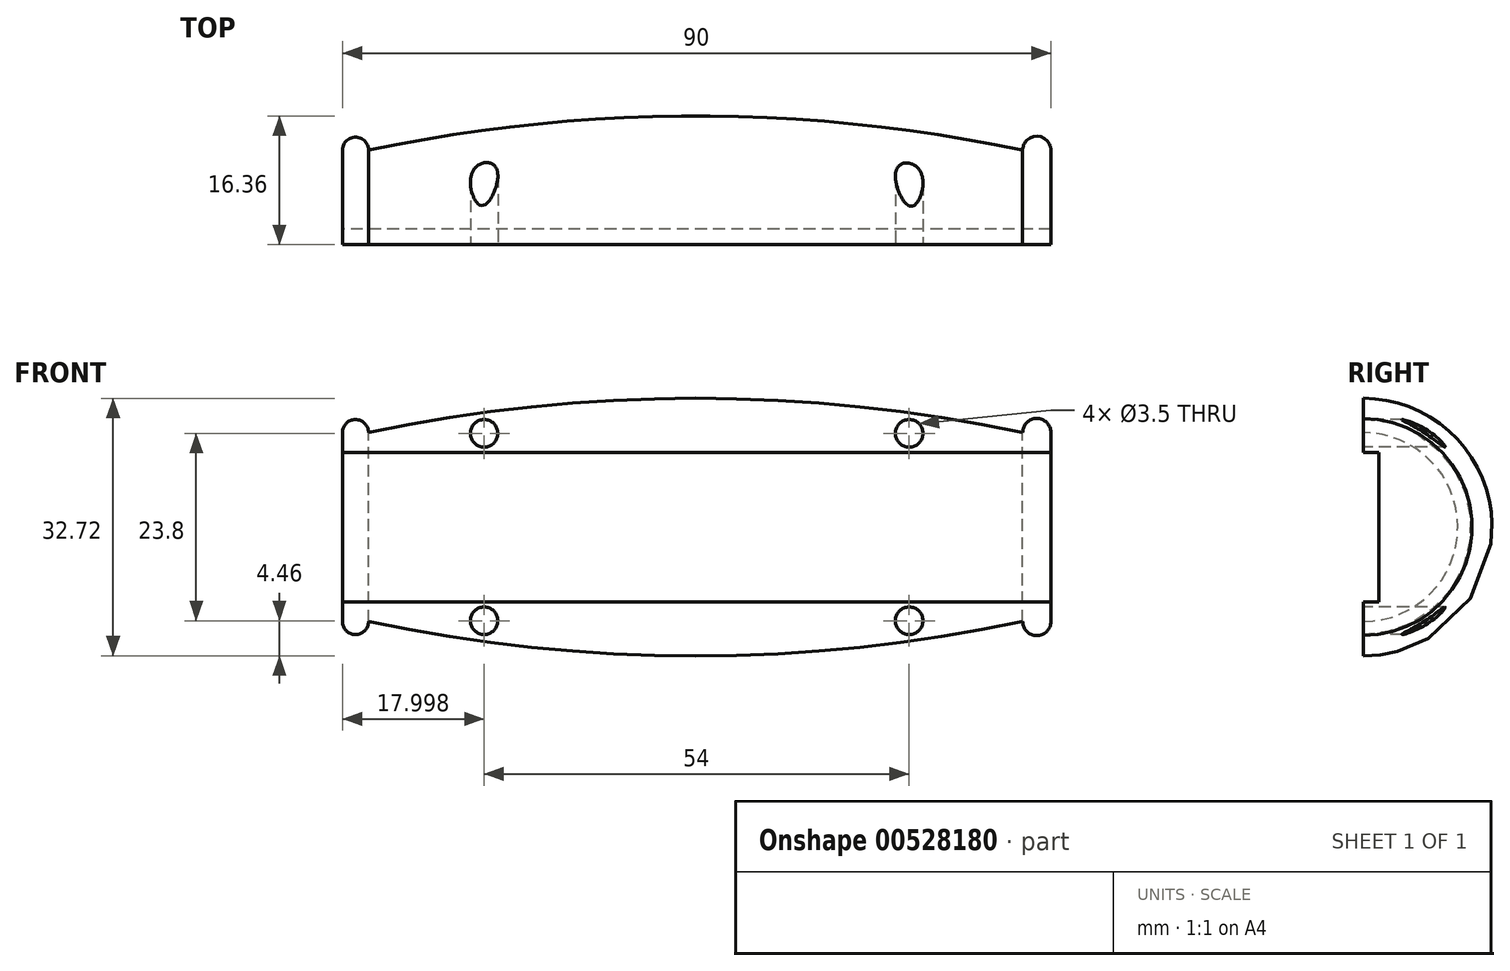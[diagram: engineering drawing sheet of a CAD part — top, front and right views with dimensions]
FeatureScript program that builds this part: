
annotation { "Feature Type Name" : "Feature", "Feature Type Description" : "" }
export const myFeature = defineFeature(function(context is Context, id is Id, definition is map)
    precondition{}
    {
        {
            var Q0;
            Q0=qCreatedBy(makeId("Front.planeOp"),FACE);
            var sketch = newSketch(context, id + "F0", { "sketchPlane" : qUnion([Q0])});
            skLineSegment(sketch, "E0", {"start": v(-128.4, 0) * mm, "end": v(-128.4, 12) * mm});
            skArc(sketch, "E1", {"start": v(-125.07, 12) * mm, "mid": v(-126.73, 13.66) * mm, "end": v(-128.4, 12) * mm});
            skLineSegment(sketch, "E2", {"start": v(-38.4, 12) * mm, "end": v(-38.4, 0) * mm});
            skLineSegment(sketch, "E3", {"start": v(-38.4, 0) * mm, "end": v(-128.4, 0) * mm});
            skArc(sketch, "E4", {"start": v(-38.4, 12) * mm, "mid": v(-40.19, 13.8) * mm, "end": v(-41.98, 12) * mm});
            skArc(sketch, "E5", {"start": v(-41.98, 12) * mm, "mid": v(-83.52, 16.36) * mm, "end": v(-125.07, 12) * mm});
            skSolve(sketch);
        }
        {
            var Q0;
            Q0=makeQuery(id+"F0.imprint","IMPRINT",FACE,{"disambiguationData":[TD([[makeQuery(id+"F0.imprint","IMPRINT",EDGE,{"derivedFrom":sQuery(id+"F0.wireOp",EDGE,"E0")}),-1.0]])]});
            var Q1;
            Q1=sQuery(id+"F0.wireOp",EDGE,"E3");
            revolve(context, id + "F1", {"entities" : qUnion([Q0]), "axis" : qUnion([Q1]), "revolveType" : RevolveType.ONE_DIRECTION, "angle" : 180 * degree});
        }
        {
            var Q0;
            Q0=makeQuery(id+"F1.opRevolve","SWEPT_FACE",FACE,{"disambiguationData":[OSD([sQuery(id+"F0.wireOp",EDGE,"E0")])]});
            var sketch = newSketch(context, id + "F2", { "sketchPlane" : qUnion([Q0])});
            skLineSegment(sketch, "E6", {"start": v(0, -9.5) * mm, "end": v(-2, -9.5) * mm});
            skLineSegment(sketch, "E7", {"start": v(-2, -9.5) * mm, "end": v(-2, 9.5) * mm});
            skLineSegment(sketch, "E8", {"start": v(-2, 9.5) * mm, "end": v(0, 9.5) * mm});
            skLineSegment(sketch, "E9", {"start": v(0, -9.5) * mm, "end": v(0, 9.5) * mm});
            skSolve(sketch);
        }
        {
            var Q0;
            Q0=makeQuery(id+"F2.imprint","IMPRINT",FACE,{"disambiguationData":[TD([[makeQuery(id+"F2.imprint","IMPRINT",EDGE,{"derivedFrom":sQuery(id+"F2.wireOp",EDGE,"E6")}),-1.0]])]});
            extrude(context, id + "F3", {"entities" : qUnion([Q0]), "operationType" : NewBodyOperationType.REMOVE, "oppositeDirection" : true, "depth" : 90 * mm, "offsetDistance" : 25 * mm});
        }
        {
            var Q0;
            {var subQ0=sQuery(id+"F0.wireOp",EDGE,"E4");var subQ1=sQuery(id+"F0.wireOp",EDGE,"E2");var subQ2=sQuery(id+"F0.wireOp",EDGE,"E1");var subQ3=sQuery(id+"F0.wireOp",EDGE,"E0");var subQ4=sQuery(id+"F0.wireOp",EDGE,"E5");Q0=makeQuery(id+"F3.boolean.opBoolean","SPLIT",FACE,{"disambiguationData":[TD([makeQuery(id+"F3.opExtrude","SWEPT_FACE",FACE,{"disambiguationData":[OSD([sQuery(id+"F2.wireOp",EDGE,"E8")])]})])],"derivedFrom":makeQuery(id+"F1.opRevolve","CAP_FACE",FACE,{"disambiguationData":[OSD([subQ3,subQ2,subQ1,sQuery(id+"F0.wireOp",EDGE,"E3"),subQ0,subQ4])],"isStart":true})});}
            var sketch = newSketch(context, id + "F4", { "sketchPlane" : qUnion([Q0])});
            skLineSegment(sketch, "E10", {"start": v(-128.4, 11.9) * mm, "end": v(-110.4, 11.9) * mm, "construction": true});
            skLineSegment(sketch, "E11", {"start": v(-128.4, 11.9) * mm, "end": v(-128.4, 9.5) * mm, "construction": true});
            skCircle(sketch, "E12", {"center": v(-110.4, 11.9) * mm, "radius": 1.75 * mm});
            skLineSegment(sketch, "E13", {"start": v(-38.4, 9.5) * mm, "end": v(-38.4, 11.9) * mm, "construction": true});
            skLineSegment(sketch, "E14", {"start": v(-38.4, 11.9) * mm, "end": v(-56.4, 11.9) * mm, "construction": true});
            skCircle(sketch, "E15", {"center": v(-56.4, 11.9) * mm, "radius": 1.75 * mm});
            skSolve(sketch);
        }
        {
            var Q0;
            {var subQ0=sQuery(id+"F0.wireOp",EDGE,"E4");var subQ1=sQuery(id+"F0.wireOp",EDGE,"E2");var subQ2=sQuery(id+"F0.wireOp",EDGE,"E1");var subQ3=sQuery(id+"F0.wireOp",EDGE,"E0");var subQ4=sQuery(id+"F0.wireOp",EDGE,"E5");Q0=makeQuery(id+"F3.boolean.opBoolean","SPLIT",FACE,{"disambiguationData":[TD([makeQuery(id+"F3.opExtrude","SWEPT_FACE",FACE,{"disambiguationData":[OSD([sQuery(id+"F2.wireOp",EDGE,"E6")])]})])],"derivedFrom":makeQuery(id+"F1.opRevolve","CAP_FACE",FACE,{"disambiguationData":[OSD([subQ3,subQ2,subQ1,sQuery(id+"F0.wireOp",EDGE,"E3"),subQ0,subQ4])],"isStart":true})});}
            var sketch = newSketch(context, id + "F5", { "sketchPlane" : qUnion([Q0])});
            skLineSegment(sketch, "E16", {"start": v(-128.4, -9.5) * mm, "end": v(-128.4, -11.9) * mm, "construction": true});
            skLineSegment(sketch, "E17", {"start": v(-128.4, -11.9) * mm, "end": v(-110.4, -11.9) * mm, "construction": true});
            skCircle(sketch, "E18", {"center": v(-110.4, -11.9) * mm, "radius": 1.75 * mm});
            skLineSegment(sketch, "E19", {"start": v(-38.4, -9.5) * mm, "end": v(-38.4, -11.9) * mm, "construction": true});
            skLineSegment(sketch, "E20", {"start": v(-38.4, -11.9) * mm, "end": v(-56.4, -11.9) * mm, "construction": true});
            skCircle(sketch, "E21", {"center": v(-56.4, -11.9) * mm, "radius": 1.75 * mm});
            skSolve(sketch);
        }
        {
            var Q0;
            Q0=makeQuery(id+"F4.imprint","IMPRINT",FACE,{"disambiguationData":[TD([[makeQuery(id+"F4.imprint","IMPRINT",EDGE,{"derivedFrom":sQuery(id+"F4.wireOp",EDGE,"E12")}),1.0]])]});
            extrude(context, id + "F6", {"entities" : qUnion([Q0]), "operationType" : NewBodyOperationType.REMOVE, "oppositeDirection" : true, "depth" : 4 * mm, "offsetDistance" : 25 * mm});
        }
        {
            var Q0;
            Q0 = qSketchRegion(id + "F4", true);
            extrude(context, id + "F7", {"entities" : qUnion([Q0]), "operationType" : NewBodyOperationType.REMOVE, "oppositeDirection" : true, "depth" : 4 * mm, "offsetDistance" : 25 * mm});
        }
        {
            var Q0;
            Q0 = qSketchRegion(id + "F5", true);
            extrude(context, id + "F8", {"entities" : qUnion([Q0]), "operationType" : NewBodyOperationType.REMOVE, "oppositeDirection" : true, "depth" : 4 * mm, "offsetDistance" : 25 * mm});
        }
        {
            var Q0;
            Q0=makeQuery(id+"F6.boolean.opBoolean","COPY",FACE,{"derivedFrom":makeQuery(id+"F6.opExtrude","CAP_FACE",FACE,{"disambiguationData":[OSD([sQuery(id+"F4.wireOp",EDGE,"E12")])],"isStart":false})});
            var Q1;
            Q1=makeQuery(id+"F8.boolean.opBoolean","COPY",FACE,{"derivedFrom":makeQuery(id+"F8.opExtrude","CAP_FACE",FACE,{"disambiguationData":[OSD([sQuery(id+"F5.wireOp",EDGE,"E18")])],"isStart":false})});
            var Q2;
            Q2=makeQuery(id+"F8.boolean.opBoolean","COPY",FACE,{"derivedFrom":makeQuery(id+"F8.opExtrude","CAP_FACE",FACE,{"disambiguationData":[OSD([sQuery(id+"F5.wireOp",EDGE,"E21")])],"isStart":false})});
            var Q3;
            Q3=makeQuery(id+"F7.boolean.opBoolean","COPY",FACE,{"derivedFrom":makeQuery(id+"F7.opExtrude","CAP_FACE",FACE,{"disambiguationData":[OSD([sQuery(id+"F4.wireOp",EDGE,"E15")])],"isStart":false})});
            extrude(context, id + "F9", {"entities" : qUnion([Q0, Q1, Q2, Q3]), "operationType" : NewBodyOperationType.REMOVE, "oppositeDirection" : true, "depth" : 100 * mm, "offsetDistance" : 25 * mm});
        }
    });
